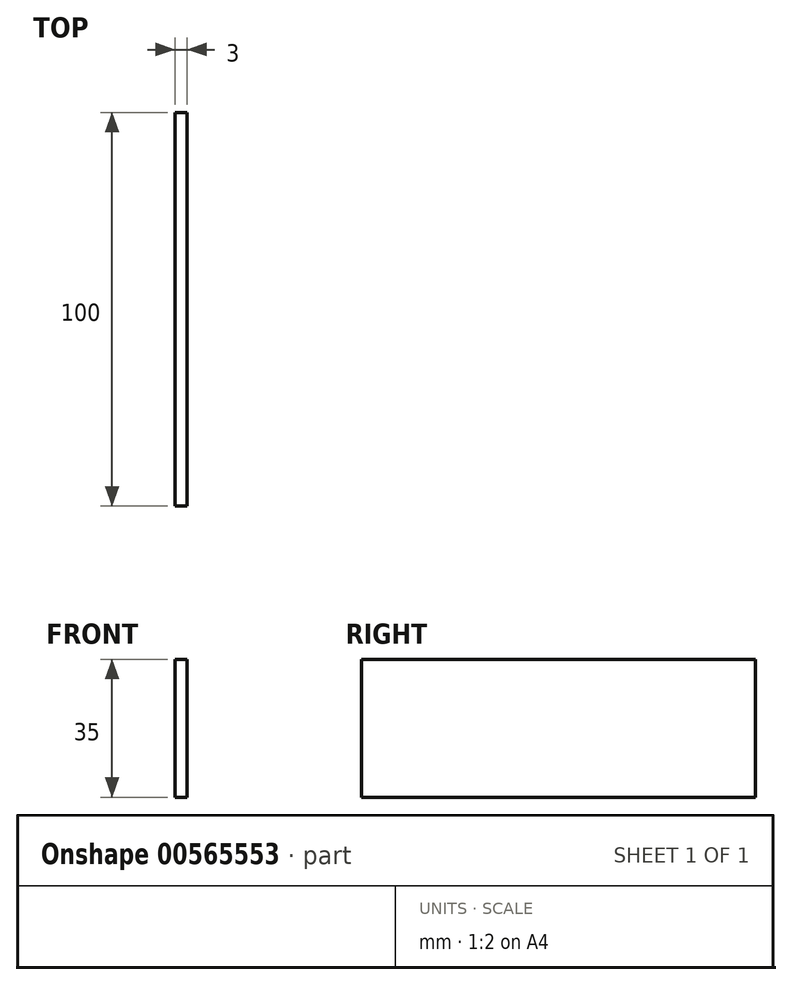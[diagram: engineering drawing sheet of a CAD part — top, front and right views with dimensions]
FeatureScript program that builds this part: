
annotation { "Feature Type Name" : "Feature", "Feature Type Description" : "" }
export const myFeature = defineFeature(function(context is Context, id is Id, definition is map)
    precondition{}
    {
        {
            var Q0;
            Q0=qCreatedBy(makeId("Right.planeOp"),FACE);
            var sketch = newSketch(context, id + "F0", { "sketchPlane" : qUnion([Q0])});
            skLineSegment(sketch, "E0.bottom", {"start": v(50, -17.5) * mm, "end": v(-50, -17.5) * mm});
            skLineSegment(sketch, "E0.top", {"start": v(50, 17.5) * mm, "end": v(-50, 17.5) * mm});
            skLineSegment(sketch, "E0.left", {"start": v(50, -17.5) * mm, "end": v(50, 17.5) * mm});
            skLineSegment(sketch, "E0.right", {"start": v(-50, -17.5) * mm, "end": v(-50, 17.5) * mm});
            skPoint(sketch, "E0.middle", {"position": v(0, 0) * mm});
            skSolve(sketch);
        }
        {
            var Q0;
            Q0 = qSketchRegion(id + "F0", true);
            extrude(context, id + "F1", {"entities" : qUnion([Q0]), "depth" : 3 * mm, "offsetDistance" : 25 * mm});
        }
    });
